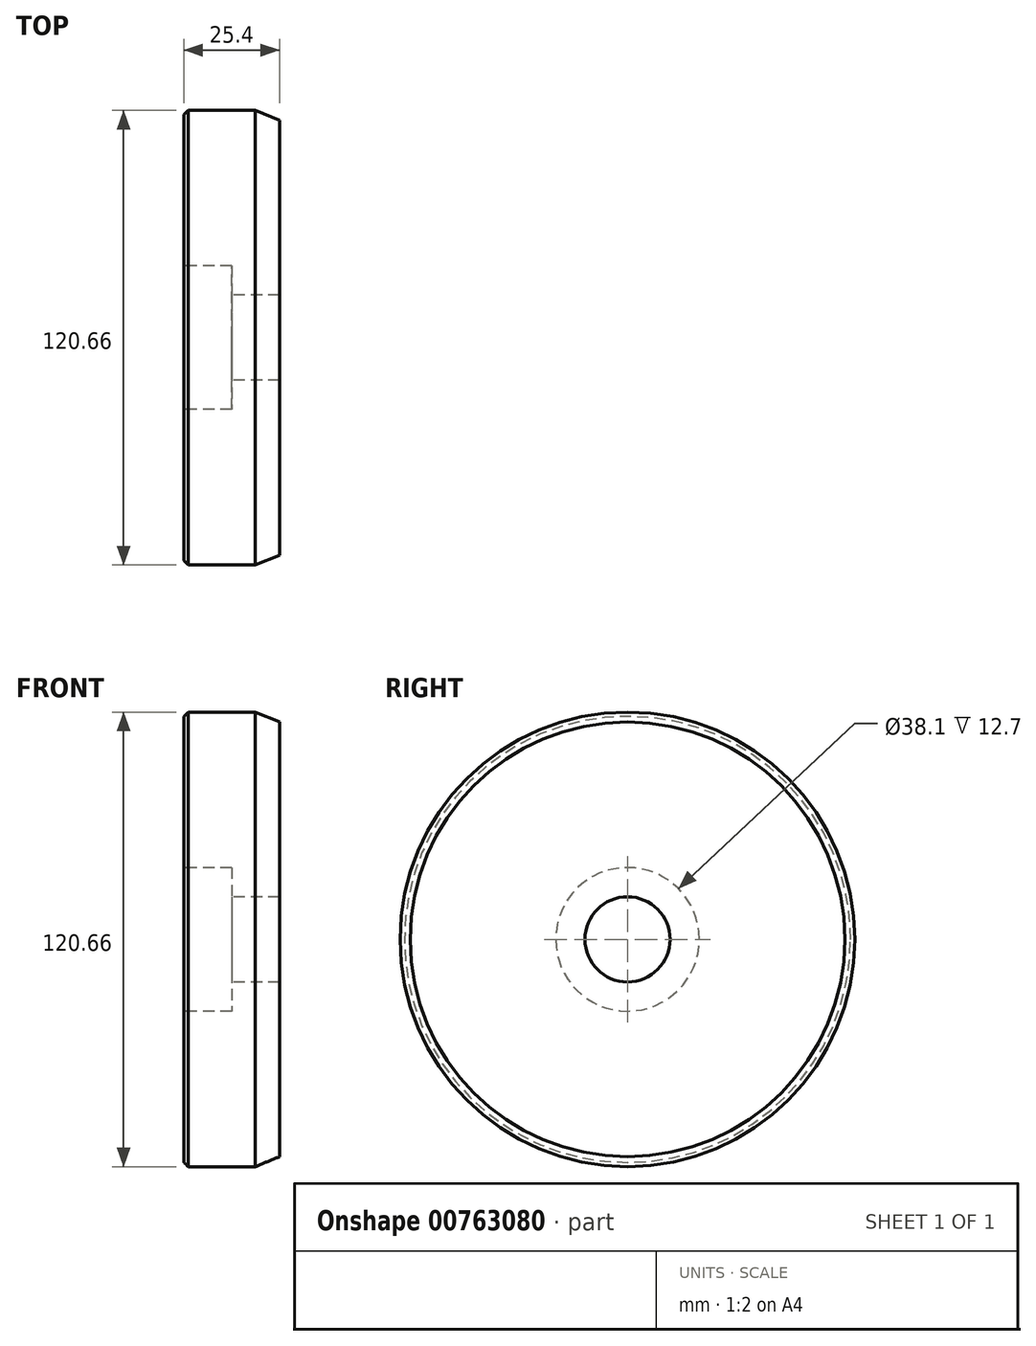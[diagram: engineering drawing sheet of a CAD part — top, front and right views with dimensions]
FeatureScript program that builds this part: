
annotation { "Feature Type Name" : "Feature", "Feature Type Description" : "" }
export const myFeature = defineFeature(function(context is Context, id is Id, definition is map)
    precondition{}
    {
        {
            var Q0;
            Q0=qCreatedBy(makeId("Right.planeOp"),FACE);
            var sketch = newSketch(context, id + "F0", { "sketchPlane" : qUnion([Q0])});
            skCircle(sketch, "E0", {"center": v(0, 0) * mm, "radius": 60.33 * mm});
            skSolve(sketch);
        }
        {
            var Q0;
            Q0=makeQuery(id+"F0.imprint","IMPRINT",FACE,{"disambiguationData":[TD([[makeQuery(id+"F0.imprint","IMPRINT",EDGE,{"derivedFrom":sQuery(id+"F0.wireOp",EDGE,"E0")}),1.0]])]});
            extrude(context, id + "F1", {"entities" : qUnion([Q0]), "oppositeDirection" : true, "depth" : 25.4 * mm, "offsetDistance" : 25.4 * mm});
        }
        {
            var Q0;
            Q0=makeQuery(id+"F1.opExtrude","CAP_EDGE",EDGE,{"disambiguationData":[OSD([sQuery(id+"F0.wireOp",EDGE,"E0")])],"isStart":false});
            var Q1;
            Q1=makeQuery(id+"F1.opExtrude","SWEPT_FACE",FACE,{"disambiguationData":[OSD([sQuery(id+"F0.wireOp",EDGE,"E0")])]});
            chamfer(context, id + "F2", {"entities" : qUnion([Q0, Q1]), "width" : 1.14 * mm, "tangentPropagation" : true});
        }
        {
            var Q0;
            Q0=makeQuery(id+"F1.opExtrude","CAP_FACE",FACE,{"disambiguationData":[OSD([sQuery(id+"F0.wireOp",EDGE,"E0")])],"isStart":false});
            var sketch = newSketch(context, id + "F3", { "sketchPlane" : qUnion([Q0])});
            skPoint(sketch, "E1", {"position": v(0, 0) * mm});
            skSolve(sketch);
        }
        {
            var Q0;
            Q0=sQuery(id+"F3.wireOp",VERTEX,"E1");
            var Q1;
            Q1=makeQuery(id+"F1.opExtrude","SWEPT_BODY",BODY,{"disambiguationData":[OSD([sQuery(id+"F0.wireOp",EDGE,"E0")])]});
            hole(context, id + "F4", {"style" : HoleStyle.C_BORE, "endStyle" : HoleEndStyle.THROUGH, "holeDiameter" : 22.6 * mm, "cBoreDiameter" : 38.1 * mm, "cBoreDepth" : 12.7 * mm, "majorDiameter" : 6.35 * mm, "tappedDepth" : 110.49 * mm, "tapClearance" : 3, "startFromSketch" : true, "locations" : qUnion([Q0]), "scope" : qUnion([Q1])});
        }
        {
            var Q0;
            {var subQ0=sQuery(id+"F0.wireOp",EDGE,"E0");Q0=makeQuery(id+"F2.opChamfer","BLEND_EDGE",EDGE,{"blendedFrom":[makeQuery(id+"F1.opExtrude","CAP_EDGE",EDGE,{"disambiguationData":[OSD([subQ0])],"isStart":true}),makeQuery(id+"F1.opExtrude","SWEPT_FACE",FACE,{"disambiguationData":[OSD([subQ0])]})],"blendedInto":[makeQuery(id+"F1.opExtrude","SWEPT_FACE",FACE,{"disambiguationData":[OSD([subQ0])]})]});}
            chamfer(context, id + "F5", {"entities" : qUnion([Q0]), "width" : 12.7 * mm, "tangentPropagation" : true});
        }
    });
